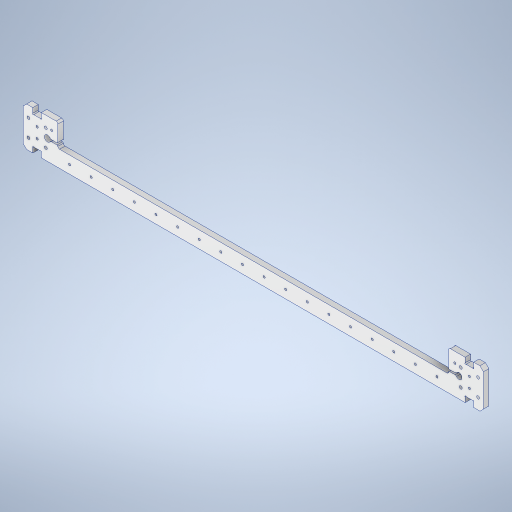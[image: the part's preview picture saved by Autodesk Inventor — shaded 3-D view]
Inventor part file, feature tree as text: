
AUTODESK INVENTOR PART (.ipt)
format: ipt  version: 2024 (Build 280153000, 153)  size: 642,560 bytes
history: native  units: mm
features: sketch x9, mirror x7, extrude x6, projected_geometry x6, hole x4, fillet x3, plane x2, chamfer x1
ambient origin geometry x8: Origin, YZ Plane, XZ Plane, XY Plane, X Axis, Y Axis, Z Axis, Center Point
bodies: Solid1 (feature_tree)
feature tree (38):
  extrude  "Extrusion1"  Depth=45.4mm
  hole  "Hole1"  [1 undecoded]
  extrude  "Extrusion8"  Depth=20.0mm
  hole  "Hole2"  [1 undecoded]
  sketch  "Sketch5"  dims[d12=3.3mm d13=6.0mm d14=4.0mm d15=2.0mm d16=90.0deg d17=8.0mm d18=20.594885mm]
  extrude  "Extrusion9"  Depth=12.0mm
  extrude  "Extrusion4"  Depth=2.0mm
  fillet  "Fillet1"  Radius=10.0mm
  mirror  "Mirror1"
  sketch  "Sketch7"  dims[d32=2.459mm d33=6.0mm d34=4.0mm d35=2.0mm d36=90.0deg d37=8.0mm d38=20.594885mm d46=2.0mm]
  extrude  "Extrusion5"  TaperAngle=0.0deg  [1 undecoded]
  mirror  "Mirror2"
  extrude  "Extrusion7"  Depth=500.0mm
  plane  "Work Plane1"
  mirror  "Mirror3"
  plane  "Work Plane2"
  mirror  "Mirror4"
  mirror  "Mirror5"
  hole  "Hole4"  [1 undecoded]
  mirror  "Mirror6"
  chamfer  "Chamfer1"  Distance=32.4mm
  fillet  "Fillet9"  Radius=6.2mm
  fillet  "Fillet10"  Radius=6.2mm
  hole  "Hole5"  [1 undecoded]
  mirror  "Mirror7"
  sketch  "Sketch1"  dims[d1=27.0mm d2=45.4mm]
  sketch  "Sketch2"  dims[d6=6.35mm d7=0.0mm d8=20.0mm]
  sketch  "Sketch3"  dims[d9=20.0mm d10=20.0mm]
  projected_geometry  "Projected Loop1"
  sketch  "Sketch4"  dims[d11=20.0mm]
  projected_geometry  "Projected Loop3"
  projected_geometry  "Projected Loop5"
  sketch  "Sketch8"  dims[d48=7.0mm d49=12.0mm]
  projected_geometry  "Projected Loop6"
  projected_geometry  "Projected Loop7"
  projected_geometry  "Projected Loop8"
  sketch  "Sketch9"  dims[d54=0.0mm d55=0.0mm d56=2.0mm d69=10.0mm d70=0.0mm]
  sketch  "Sketch10"  dims[d77=1.5mm d80=0.0mm d81=0.0mm d97=500.0mm d98=19.2mm d100=32.4mm d102=6.2mm d103=6.2mm d104=10.0mm d105=0.0mm d106=180.0mm d108=25.0mm d109=10.0mm d111=10.0mm d113=13.5mm d114=12.0mm d115=10.0mm d116=0.0mm d117=9.75mm d118=32.4mm d119=24.0mm d120=20.7mm d121=2.459mm d122=6.0mm d123=4.0mm d124=2.0mm d125=90.0deg d126=8.0mm d127=20.594885mm d128=4.0mm d129=2.0mm d130=45.0deg d131=2.0mm d132=1.0mm d133=12.0mm d134=2.459mm d135=6.0mm d136=4.0mm d137=2.0mm d138=90.0deg d139=8.0mm d140=20.594885mm d141=0.4mm d142=0.4mm]
note: 5 required parameter values undecoded (feature->parameter linkage not recoverable at this tier; creation-order binding heuristic only, values carry confidence <= 0.55)
